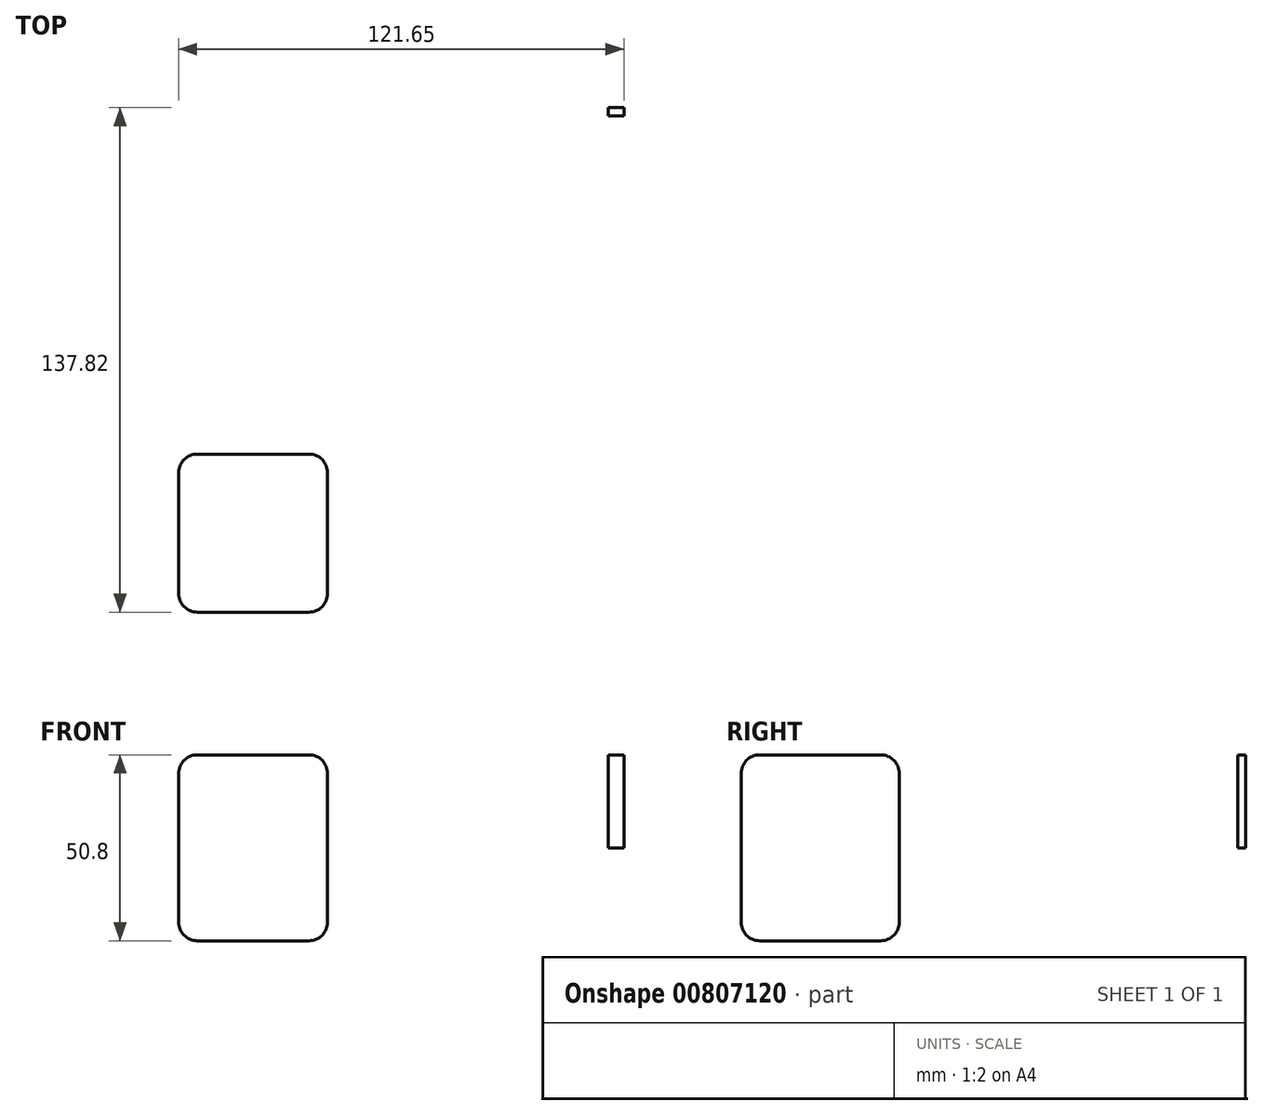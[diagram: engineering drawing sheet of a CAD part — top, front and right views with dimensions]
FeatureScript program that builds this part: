
annotation { "Feature Type Name" : "Feature", "Feature Type Description" : "" }
export const myFeature = defineFeature(function(context is Context, id is Id, definition is map)
    precondition{}
    {
        {
            var Q0;
            Q0=qCreatedBy(makeId("Top.planeOp"),FACE);
            var sketch = newSketch(context, id + "F0", { "sketchPlane" : qUnion([Q0])});
            skLineSegment(sketch, "E0.bottom", {"start": v(-54.52, 43.17) * mm, "end": v(-13.84, 43.17) * mm});
            skLineSegment(sketch, "E0.top", {"start": v(-54.52, 0) * mm, "end": v(-13.84, 0) * mm});
            skLineSegment(sketch, "E0.left", {"start": v(-54.52, 43.17) * mm, "end": v(-54.52, 0) * mm});
            skLineSegment(sketch, "E0.right", {"start": v(-13.84, 43.17) * mm, "end": v(-13.84, 0) * mm});
            skLineSegment(sketch, "E1.bottom", {"start": v(67.13, 135.63) * mm, "end": v(62.78, 135.63) * mm});
            skLineSegment(sketch, "E1.top", {"start": v(67.13, 137.82) * mm, "end": v(62.78, 137.82) * mm});
            skLineSegment(sketch, "E1.left", {"start": v(67.13, 135.63) * mm, "end": v(67.13, 137.82) * mm});
            skLineSegment(sketch, "E1.right", {"start": v(62.78, 135.63) * mm, "end": v(62.78, 137.82) * mm});
            skSolve(sketch);
        }
        {
            var Q0;
            Q0 = qSketchRegion(id + "F0", true);
            extrude(context, id + "F1", {"entities" : qUnion([Q0]), "oppositeDirection" : true, "depth" : 25.4 * mm, "offsetDistance" : 25.4 * mm});
        }
        {
            var Q0;
            Q0=makeQuery(id+"F1.opExtrude","CAP_FACE",FACE,{"disambiguationData":[OSD([sQuery(id+"F0.wireOp",EDGE,"E0.bottom"),sQuery(id+"F0.wireOp",EDGE,"E0.top"),sQuery(id+"F0.wireOp",EDGE,"E0.left"),sQuery(id+"F0.wireOp",EDGE,"E0.right")])],"isStart":false});
            extrude(context, id + "F2", {"entities" : qUnion([Q0]), "operationType" : NewBodyOperationType.ADD, "depth" : 25.4 * mm, "offsetDistance" : 25.4 * mm});
        }
        {
            var Q0;
            Q0=makeQuery(id+"F2.opExtrude","CAP_EDGE",EDGE,{"disambiguationData":[OSD([sQuery(id+"F0.wireOp",EDGE,"E0.top")])],"isStart":false});
            fillet(context, id + "F3", {"entities" : qUnion([Q0]), "radius" : 5.08 * mm, "tangentPropagation" : true, "allowEdgeOverflow" : false});
        }
        {
            var Q0;
            {var subQ0=sQuery(id+"F0.wireOp",EDGE,"E0.left");Q0=makeQuery(id+"F2.boolean.opBoolean","MERGE",FACE,{"derivedFrom":[makeQuery(id+"F1.opExtrude","SWEPT_FACE",FACE,{"disambiguationData":[OSD([subQ0])]}),makeQuery(id+"F2.opExtrude","SWEPT_FACE",FACE,{"disambiguationData":[OSD([subQ0])]})]});}
            fillet(context, id + "F4", {"entities" : qUnion([Q0]), "radius" : 5.08 * mm, "tangentPropagation" : true, "allowEdgeOverflow" : false});
        }
        {
            var Q0;
            Q0=makeQuery(id+"F2.opExtrude","CAP_FACE",FACE,{"disambiguationData":[OSD([sQuery(id+"F0.wireOp",EDGE,"E0.bottom"),sQuery(id+"F0.wireOp",EDGE,"E0.top"),sQuery(id+"F0.wireOp",EDGE,"E0.left"),sQuery(id+"F0.wireOp",EDGE,"E0.right")])],"isStart":false});
            fillet(context, id + "F5", {"entities" : qUnion([Q0]), "radius" : 5.08 * mm, "tangentPropagation" : true, "allowEdgeOverflow" : false});
        }
        {
            var Q0;
            Q0=makeQuery(id+"F1.opExtrude","CAP_FACE",FACE,{"disambiguationData":[OSD([sQuery(id+"F0.wireOp",EDGE,"E0.bottom"),sQuery(id+"F0.wireOp",EDGE,"E0.top"),sQuery(id+"F0.wireOp",EDGE,"E0.left"),sQuery(id+"F0.wireOp",EDGE,"E0.right")])],"isStart":true});
            var Q1;
            {var subQ0=sQuery(id+"F0.wireOp",EDGE,"E0.right");Q1=makeQuery(id+"F2.boolean.opBoolean","MERGE",FACE,{"derivedFrom":[makeQuery(id+"F1.opExtrude","SWEPT_FACE",FACE,{"disambiguationData":[OSD([subQ0])]}),makeQuery(id+"F2.opExtrude","SWEPT_FACE",FACE,{"disambiguationData":[OSD([subQ0])]})]});}
            var Q2;
            Q2=makeQuery(id+"F2.opExtrude","CAP_FACE",FACE,{"disambiguationData":[OSD([sQuery(id+"F0.wireOp",EDGE,"E0.bottom"),sQuery(id+"F0.wireOp",EDGE,"E0.top"),sQuery(id+"F0.wireOp",EDGE,"E0.left"),sQuery(id+"F0.wireOp",EDGE,"E0.right")])],"isStart":false});
            fillet(context, id + "F6", {"entities" : qUnion([Q0, Q1, Q2]), "radius" : 5.08 * mm, "tangentPropagation" : true, "allowEdgeOverflow" : false});
        }
    });
